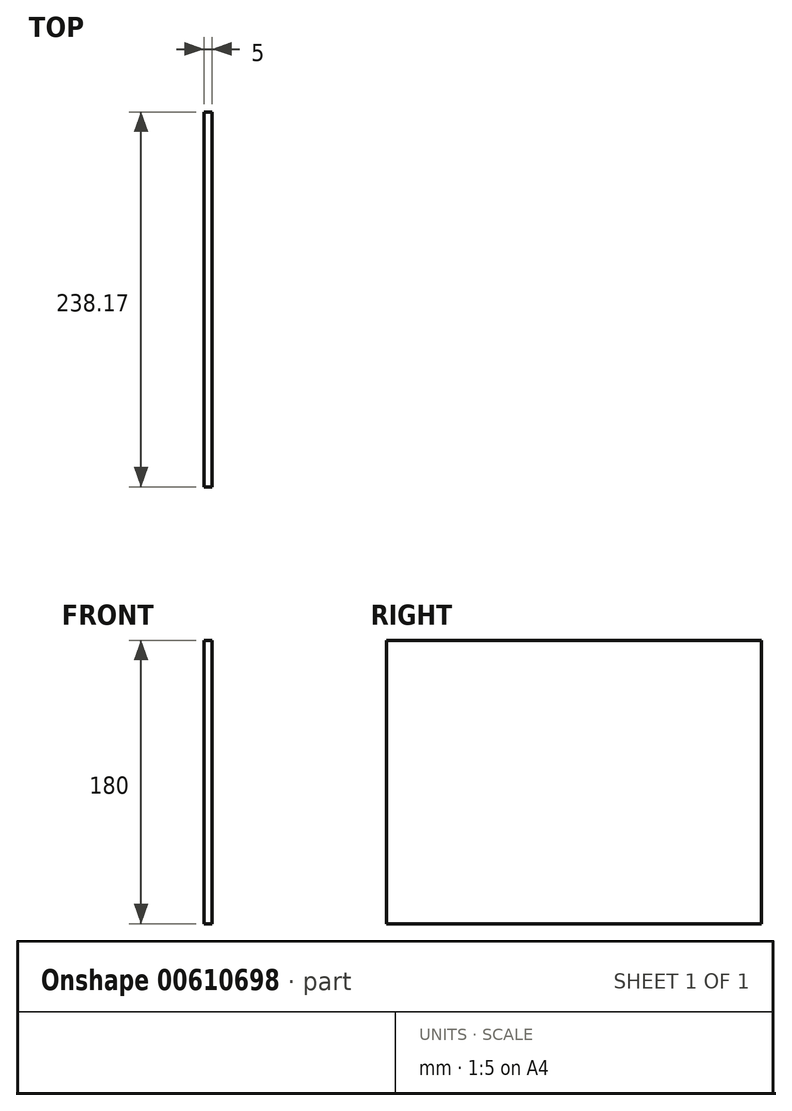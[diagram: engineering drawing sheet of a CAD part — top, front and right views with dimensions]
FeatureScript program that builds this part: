
annotation { "Feature Type Name" : "Feature", "Feature Type Description" : "" }
export const myFeature = defineFeature(function(context is Context, id is Id, definition is map)
    precondition{}
    {
        {
            var Q0;
            Q0=qCreatedBy(makeId("Right.planeOp"),FACE);
            var sketch = newSketch(context, id + "F0", { "sketchPlane" : qUnion([Q0])});
            skLineSegment(sketch, "E0.bottom", {"start": v(0, 0) * mm, "end": v(238.17, 0) * mm});
            skLineSegment(sketch, "E0.top", {"start": v(0, 180) * mm, "end": v(238.17, 180) * mm});
            skLineSegment(sketch, "E0.left", {"start": v(0, 0) * mm, "end": v(0, 180) * mm});
            skLineSegment(sketch, "E0.right", {"start": v(238.17, 0) * mm, "end": v(238.17, 180) * mm});
            skSolve(sketch);
        }
        {
            var Q0;
            Q0 = qSketchRegion(id + "F0", true);
            extrude(context, id + "F1", {"entities" : qUnion([Q0]), "depth" : 5 * mm, "offsetDistance" : 25 * mm});
        }
    });
